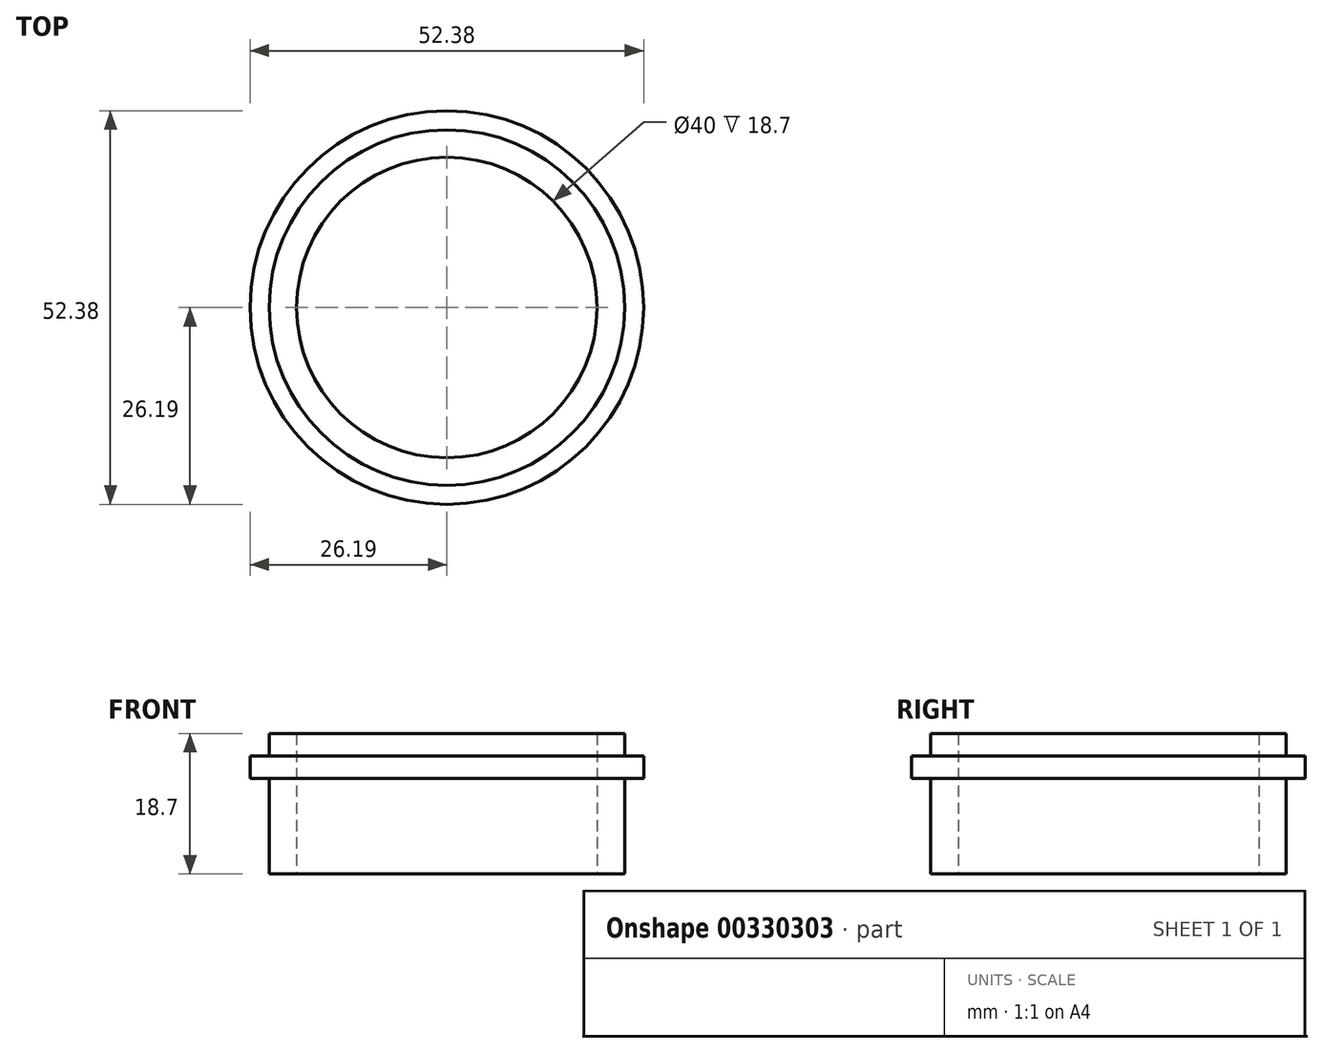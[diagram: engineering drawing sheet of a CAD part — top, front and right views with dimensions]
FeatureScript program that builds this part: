
annotation { "Feature Type Name" : "Feature", "Feature Type Description" : "" }
export const myFeature = defineFeature(function(context is Context, id is Id, definition is map)
    precondition{}
    {
        {
            var Q0;
            Q0=qCreatedBy(makeId("Top.planeOp"),FACE);
            var sketch = newSketch(context, id + "F0", { "sketchPlane" : qUnion([Q0])});
            skCircle(sketch, "E0", {"center": v(0, 0) * mm, "radius": 20 * mm});
            skCircle(sketch, "E1", {"center": v(0, 0) * mm, "radius": 75 * mm});
            skSolve(sketch);
        }
        {
            var Q0;
            Q0=qCreatedBy(makeId("Top.planeOp"),FACE);
            var sketch = newSketch(context, id + "F1", { "sketchPlane" : qUnion([Q0])});
            skCircle(sketch, "E2.0", {"center": v(0, 0) * mm, "radius": 20 * mm});
            skCircle(sketch, "E3", {"center": v(0, 0) * mm, "radius": 26.19 * mm});
            skCircle(sketch, "E4", {"center": v(0, 0) * mm, "radius": 23.65 * mm});
            skSolve(sketch);
        }
        {
            var Q0;
            Q0=makeQuery(id+"F1.imprint","IMPRINT",FACE,{"disambiguationData":[TD([[makeQuery(id+"F1.imprint","IMPRINT",EDGE,{"derivedFrom":sQuery(id+"F1.wireOp",EDGE,"E2.0")}),-1.0]])]});
            extrude(context, id + "F2", {"entities" : qUnion([Q0]), "depth" : 3 * mm, "hasSecondDirection" : true, "secondDirectionOppositeDirection" : true, "secondDirectionDepth" : 15.7 * mm});
        }
        {
            var Q0;
            Q0=makeQuery(id+"F1.imprint","IMPRINT",FACE,{"disambiguationData":[TD([[makeQuery(id+"F1.imprint","IMPRINT",EDGE,{"derivedFrom":sQuery(id+"F1.wireOp",EDGE,"E3")}),1.0]])]});
            var Q1;
            Q1=makeQuery(id+"F1.imprint","IMPRINT",FACE,{"disambiguationData":[TD([[makeQuery(id+"F1.imprint","IMPRINT",EDGE,{"derivedFrom":sQuery(id+"F1.wireOp",EDGE,"E2.0")}),-1.0]])]});
            extrude(context, id + "F3", {"entities" : qUnion([Q0, Q1]), "operationType" : NewBodyOperationType.ADD, "oppositeDirection" : true, "depth" : 3 * mm});
        }
    });
